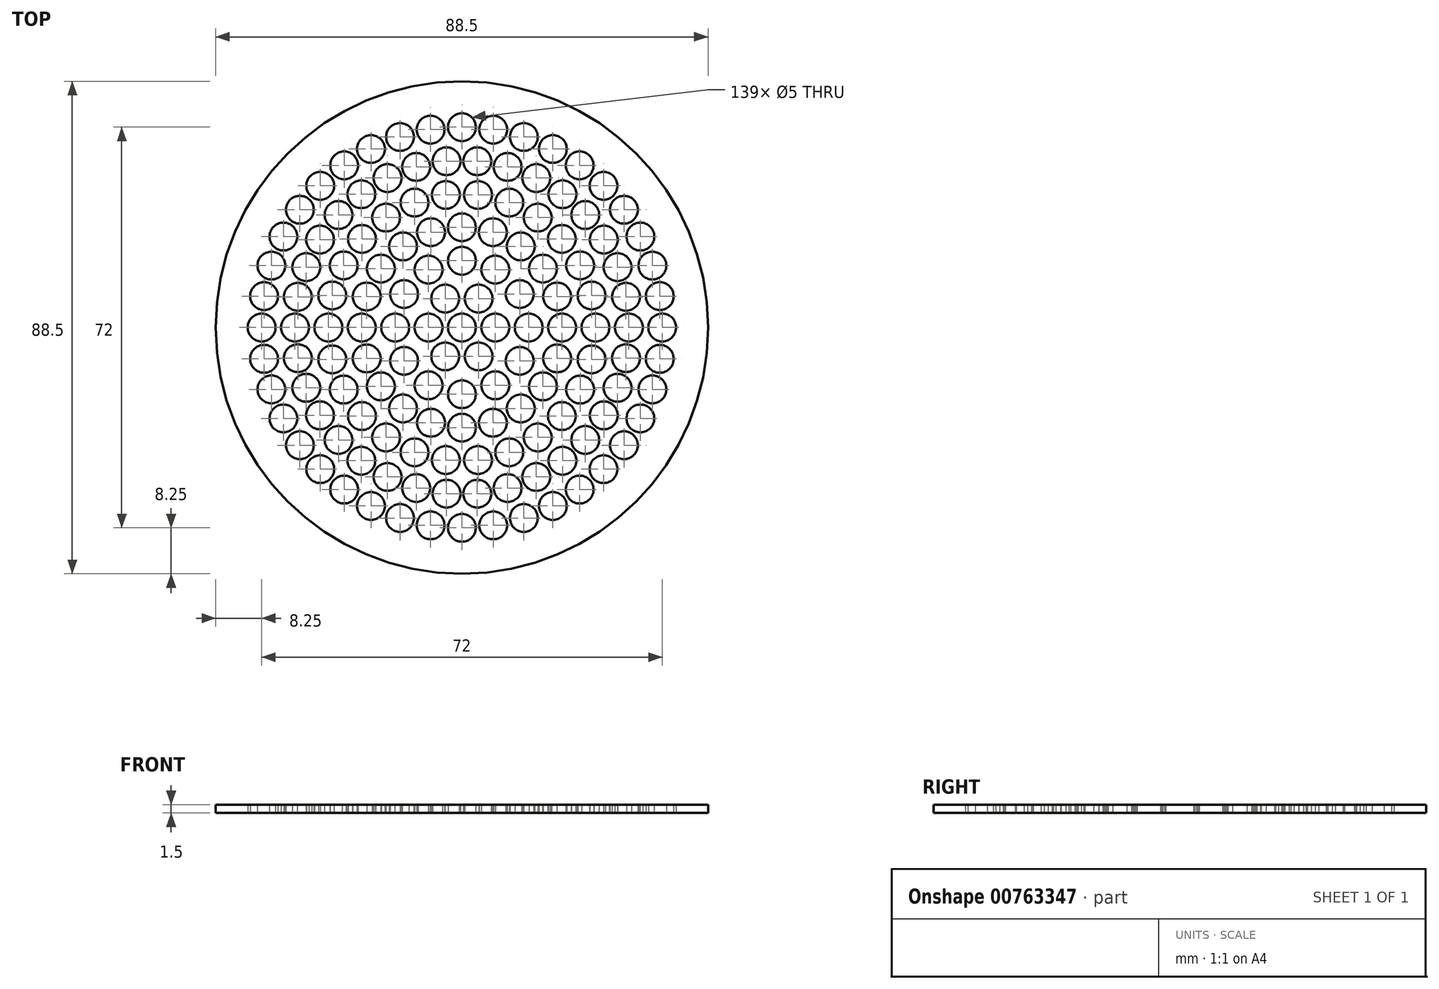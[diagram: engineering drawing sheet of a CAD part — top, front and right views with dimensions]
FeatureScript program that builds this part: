
annotation { "Feature Type Name" : "Feature", "Feature Type Description" : "" }
export const myFeature = defineFeature(function(context is Context, id is Id, definition is map)
    precondition{}
    {
        {
            var Q0;
            Q0=qCreatedBy(makeId("Top.planeOp"),FACE);
            var sketch = newSketch(context, id + "F0", { "sketchPlane" : qUnion([Q0])});
            skCircle(sketch, "E0", {"center": v(0, 0) * mm, "radius": 44.25 * mm});
            skCircle(sketch, "E1", {"center": v(0, 0) * mm, "radius": 2.5 * mm});
            skCircle(sketch, "E2.1.0.0", {"center": v(6, 0) * mm, "radius": 2.5 * mm});
            skCircle(sketch, "E2.2.0.0", {"center": v(12, 0) * mm, "radius": 2.5 * mm});
            skCircle(sketch, "E2.3.0.0", {"center": v(18, 0) * mm, "radius": 2.5 * mm});
            skCircle(sketch, "E2.4.0.0", {"center": v(24, 0) * mm, "radius": 2.5 * mm});
            skCircle(sketch, "E2.5.0.0", {"center": v(30, 0) * mm, "radius": 2.5 * mm});
            skCircle(sketch, "E2.6.0.0", {"center": v(36, 0) * mm, "radius": 2.5 * mm});
            skLineSegment(sketch, "E2.direction1", {"start": v(0, 0) * mm, "end": v(6, 0) * mm, "construction": true});
            skCircle(sketch, "E3.1.0", {"center": v(3, 5.2) * mm, "radius": 2.5 * mm});
            skCircle(sketch, "E3.2.0", {"center": v(-3, 5.2) * mm, "radius": 2.5 * mm});
            skCircle(sketch, "E3.3.0", {"center": v(-6, 0) * mm, "radius": 2.5 * mm});
            skCircle(sketch, "E3.4.0", {"center": v(-3, -5.2) * mm, "radius": 2.5 * mm});
            skCircle(sketch, "E4.1.0", {"center": v(10.4, 6) * mm, "radius": 2.5 * mm});
            skCircle(sketch, "E4.2.0", {"center": v(6, 10.4) * mm, "radius": 2.5 * mm});
            skCircle(sketch, "E4.3.0", {"center": v(0, 12) * mm, "radius": 2.5 * mm});
            skCircle(sketch, "E4.4.0", {"center": v(-6, 10.4) * mm, "radius": 2.5 * mm});
            skCircle(sketch, "E4.5.0", {"center": v(-10.4, 6) * mm, "radius": 2.5 * mm});
            skCircle(sketch, "E4.6.0", {"center": v(-12, 0) * mm, "radius": 2.5 * mm});
            skCircle(sketch, "E4.7.0", {"center": v(-10.4, -6) * mm, "radius": 2.5 * mm});
            skCircle(sketch, "E4.8.0", {"center": v(-6, -10.4) * mm, "radius": 2.5 * mm});
            skCircle(sketch, "E4.9.0", {"center": v(0, -12) * mm, "radius": 2.5 * mm});
            skCircle(sketch, "E5.1.5.0", {"center": v(3, -5.2) * mm, "radius": 2.5 * mm});
            skCircle(sketch, "E6.1.10.0", {"center": v(6, -10.4) * mm, "radius": 2.5 * mm});
            skCircle(sketch, "E6.1.11.0", {"center": v(10.4, -6) * mm, "radius": 2.5 * mm});
            skCircle(sketch, "E7.1.0", {"center": v(17.12, 5.56) * mm, "radius": 2.5 * mm});
            skCircle(sketch, "E7.2.0", {"center": v(14.56, 10.58) * mm, "radius": 2.5 * mm});
            skCircle(sketch, "E7.3.0", {"center": v(10.58, 14.56) * mm, "radius": 2.5 * mm});
            skCircle(sketch, "E7.4.0", {"center": v(5.56, 17.12) * mm, "radius": 2.5 * mm});
            skCircle(sketch, "E7.5.0", {"center": v(0, 18) * mm, "radius": 2.5 * mm});
            skCircle(sketch, "E7.6.0", {"center": v(-5.56, 17.12) * mm, "radius": 2.5 * mm});
            skCircle(sketch, "E7.7.0", {"center": v(-10.58, 14.56) * mm, "radius": 2.5 * mm});
            skCircle(sketch, "E7.8.0", {"center": v(-14.56, 10.58) * mm, "radius": 2.5 * mm});
            skCircle(sketch, "E7.9.0", {"center": v(-17.12, 5.56) * mm, "radius": 2.5 * mm});
            skCircle(sketch, "E7.10.0", {"center": v(-18, 0) * mm, "radius": 2.5 * mm});
            skCircle(sketch, "E7.11.0", {"center": v(-17.12, -5.56) * mm, "radius": 2.5 * mm});
            skCircle(sketch, "E7.12.0", {"center": v(-14.56, -10.58) * mm, "radius": 2.5 * mm});
            skCircle(sketch, "E7.13.0", {"center": v(-10.58, -14.56) * mm, "radius": 2.5 * mm});
            skCircle(sketch, "E7.14.0", {"center": v(-5.56, -17.12) * mm, "radius": 2.5 * mm});
            skCircle(sketch, "E7.15.0", {"center": v(0, -18) * mm, "radius": 2.5 * mm});
            skCircle(sketch, "E7.16.0", {"center": v(5.56, -17.12) * mm, "radius": 2.5 * mm});
            skCircle(sketch, "E7.17.0", {"center": v(10.58, -14.56) * mm, "radius": 2.5 * mm});
            skCircle(sketch, "E7.18.0", {"center": v(14.56, -10.58) * mm, "radius": 2.5 * mm});
            skCircle(sketch, "E7.19.0", {"center": v(17.12, -5.56) * mm, "radius": 2.5 * mm});
            skCircle(sketch, "E8.1.0", {"center": v(23.3, 5.74) * mm, "radius": 2.5 * mm});
            skCircle(sketch, "E8.2.0", {"center": v(21.25, 11.15) * mm, "radius": 2.5 * mm});
            skCircle(sketch, "E8.3.0", {"center": v(17.96, 15.91) * mm, "radius": 2.5 * mm});
            skCircle(sketch, "E8.4.0", {"center": v(13.63, 19.75) * mm, "radius": 2.5 * mm});
            skCircle(sketch, "E8.5.0", {"center": v(8.51, 22.44) * mm, "radius": 2.5 * mm});
            skCircle(sketch, "E8.6.0", {"center": v(2.9, 23.83) * mm, "radius": 2.5 * mm});
            skCircle(sketch, "E8.7.0", {"center": v(-2.9, 23.83) * mm, "radius": 2.5 * mm});
            skCircle(sketch, "E8.8.0", {"center": v(-8.51, 22.44) * mm, "radius": 2.5 * mm});
            skCircle(sketch, "E8.9.0", {"center": v(-13.63, 19.75) * mm, "radius": 2.5 * mm});
            skCircle(sketch, "E8.10.0", {"center": v(-17.96, 15.91) * mm, "radius": 2.5 * mm});
            skCircle(sketch, "E8.11.0", {"center": v(-21.25, 11.15) * mm, "radius": 2.5 * mm});
            skCircle(sketch, "E8.12.0", {"center": v(-23.3, 5.74) * mm, "radius": 2.5 * mm});
            skCircle(sketch, "E8.13.0", {"center": v(-24, 0) * mm, "radius": 2.5 * mm});
            skCircle(sketch, "E8.14.0", {"center": v(-23.3, -5.74) * mm, "radius": 2.5 * mm});
            skCircle(sketch, "E8.15.0", {"center": v(-21.25, -11.15) * mm, "radius": 2.5 * mm});
            skCircle(sketch, "E8.16.0", {"center": v(-17.96, -15.91) * mm, "radius": 2.5 * mm});
            skCircle(sketch, "E8.17.0", {"center": v(-13.63, -19.75) * mm, "radius": 2.5 * mm});
            skCircle(sketch, "E8.18.0", {"center": v(-8.51, -22.44) * mm, "radius": 2.5 * mm});
            skCircle(sketch, "E8.19.0", {"center": v(-2.9, -23.83) * mm, "radius": 2.5 * mm});
            skCircle(sketch, "E8.20.0", {"center": v(2.9, -23.83) * mm, "radius": 2.5 * mm});
            skCircle(sketch, "E8.21.0", {"center": v(8.51, -22.44) * mm, "radius": 2.5 * mm});
            skCircle(sketch, "E8.22.0", {"center": v(13.63, -19.75) * mm, "radius": 2.5 * mm});
            skCircle(sketch, "E8.23.0", {"center": v(17.96, -15.91) * mm, "radius": 2.5 * mm});
            skCircle(sketch, "E8.24.0", {"center": v(21.25, -11.15) * mm, "radius": 2.5 * mm});
            skCircle(sketch, "E8.25.0", {"center": v(23.3, -5.74) * mm, "radius": 2.5 * mm});
            skCircle(sketch, "E9.1.0", {"center": v(29.49, 5.51) * mm, "radius": 2.5 * mm});
            skCircle(sketch, "E9.2.0", {"center": v(27.97, 10.84) * mm, "radius": 2.5 * mm});
            skCircle(sketch, "E9.3.0", {"center": v(25.5, 15.8) * mm, "radius": 2.5 * mm});
            skCircle(sketch, "E9.4.0", {"center": v(22.17, 20.21) * mm, "radius": 2.5 * mm});
            skCircle(sketch, "E9.5.0", {"center": v(18.08, 23.94) * mm, "radius": 2.5 * mm});
            skCircle(sketch, "E9.6.0", {"center": v(13.37, 26.85) * mm, "radius": 2.5 * mm});
            skCircle(sketch, "E9.7.0", {"center": v(8.2, 28.85) * mm, "radius": 2.5 * mm});
            skCircle(sketch, "E9.8.0", {"center": v(2.77, 29.87) * mm, "radius": 2.5 * mm});
            skCircle(sketch, "E9.9.0", {"center": v(-2.77, 29.87) * mm, "radius": 2.5 * mm});
            skCircle(sketch, "E9.10.0", {"center": v(-8.2, 28.85) * mm, "radius": 2.5 * mm});
            skCircle(sketch, "E9.11.0", {"center": v(-13.37, 26.85) * mm, "radius": 2.5 * mm});
            skCircle(sketch, "E9.12.0", {"center": v(-18.08, 23.94) * mm, "radius": 2.5 * mm});
            skCircle(sketch, "E9.13.0", {"center": v(-22.17, 20.21) * mm, "radius": 2.5 * mm});
            skCircle(sketch, "E9.14.0", {"center": v(-25.5, 15.8) * mm, "radius": 2.5 * mm});
            skCircle(sketch, "E9.15.0", {"center": v(-27.97, 10.84) * mm, "radius": 2.5 * mm});
            skCircle(sketch, "E9.16.0", {"center": v(-29.49, 5.51) * mm, "radius": 2.5 * mm});
            skCircle(sketch, "E9.17.0", {"center": v(-30, 0) * mm, "radius": 2.5 * mm});
            skCircle(sketch, "E9.18.0", {"center": v(-29.49, -5.51) * mm, "radius": 2.5 * mm});
            skCircle(sketch, "E9.19.0", {"center": v(-27.97, -10.84) * mm, "radius": 2.5 * mm});
            skCircle(sketch, "E9.20.0", {"center": v(-25.5, -15.8) * mm, "radius": 2.5 * mm});
            skCircle(sketch, "E9.21.0", {"center": v(-22.17, -20.21) * mm, "radius": 2.5 * mm});
            skCircle(sketch, "E9.22.0", {"center": v(-18.08, -23.94) * mm, "radius": 2.5 * mm});
            skCircle(sketch, "E9.23.0", {"center": v(-13.37, -26.85) * mm, "radius": 2.5 * mm});
            skCircle(sketch, "E9.24.0", {"center": v(-8.2, -28.85) * mm, "radius": 2.5 * mm});
            skCircle(sketch, "E9.25.0", {"center": v(-2.77, -29.87) * mm, "radius": 2.5 * mm});
            skCircle(sketch, "E9.26.0", {"center": v(2.77, -29.87) * mm, "radius": 2.5 * mm});
            skCircle(sketch, "E9.27.0", {"center": v(8.2, -28.85) * mm, "radius": 2.5 * mm});
            skCircle(sketch, "E9.28.0", {"center": v(13.37, -26.85) * mm, "radius": 2.5 * mm});
            skCircle(sketch, "E9.29.0", {"center": v(18.08, -23.94) * mm, "radius": 2.5 * mm});
            skCircle(sketch, "E9.30.0", {"center": v(22.17, -20.21) * mm, "radius": 2.5 * mm});
            skCircle(sketch, "E9.31.0", {"center": v(25.5, -15.8) * mm, "radius": 2.5 * mm});
            skCircle(sketch, "E9.32.0", {"center": v(27.97, -10.84) * mm, "radius": 2.5 * mm});
            skCircle(sketch, "E9.33.0", {"center": v(29.49, -5.51) * mm, "radius": 2.5 * mm});
            skCircle(sketch, "E10.1.0", {"center": v(35.56, 5.63) * mm, "radius": 2.5 * mm});
            skCircle(sketch, "E10.2.0", {"center": v(34.24, 11.12) * mm, "radius": 2.5 * mm});
            skCircle(sketch, "E10.3.0", {"center": v(32.08, 16.34) * mm, "radius": 2.5 * mm});
            skCircle(sketch, "E10.4.0", {"center": v(29.12, 21.16) * mm, "radius": 2.5 * mm});
            skCircle(sketch, "E10.5.0", {"center": v(25.46, 25.46) * mm, "radius": 2.5 * mm});
            skCircle(sketch, "E10.6.0", {"center": v(21.16, 29.12) * mm, "radius": 2.5 * mm});
            skCircle(sketch, "E10.7.0", {"center": v(16.34, 32.08) * mm, "radius": 2.5 * mm});
            skCircle(sketch, "E10.8.0", {"center": v(11.12, 34.24) * mm, "radius": 2.5 * mm});
            skCircle(sketch, "E10.9.0", {"center": v(5.63, 35.56) * mm, "radius": 2.5 * mm});
            skCircle(sketch, "E10.10.0", {"center": v(0, 36) * mm, "radius": 2.5 * mm});
            skCircle(sketch, "E10.11.0", {"center": v(-5.63, 35.56) * mm, "radius": 2.5 * mm});
            skCircle(sketch, "E10.12.0", {"center": v(-11.12, 34.24) * mm, "radius": 2.5 * mm});
            skCircle(sketch, "E10.13.0", {"center": v(-16.34, 32.08) * mm, "radius": 2.5 * mm});
            skCircle(sketch, "E10.14.0", {"center": v(-21.16, 29.12) * mm, "radius": 2.5 * mm});
            skCircle(sketch, "E10.15.0", {"center": v(-25.46, 25.46) * mm, "radius": 2.5 * mm});
            skCircle(sketch, "E10.16.0", {"center": v(-29.12, 21.16) * mm, "radius": 2.5 * mm});
            skCircle(sketch, "E10.17.0", {"center": v(-32.08, 16.34) * mm, "radius": 2.5 * mm});
            skCircle(sketch, "E10.18.0", {"center": v(-34.24, 11.12) * mm, "radius": 2.5 * mm});
            skCircle(sketch, "E10.19.0", {"center": v(-35.56, 5.63) * mm, "radius": 2.5 * mm});
            skCircle(sketch, "E10.20.0", {"center": v(-36, 0) * mm, "radius": 2.5 * mm});
            skCircle(sketch, "E10.21.0", {"center": v(-35.56, -5.63) * mm, "radius": 2.5 * mm});
            skCircle(sketch, "E10.22.0", {"center": v(-34.24, -11.12) * mm, "radius": 2.5 * mm});
            skCircle(sketch, "E10.23.0", {"center": v(-32.08, -16.34) * mm, "radius": 2.5 * mm});
            skCircle(sketch, "E10.24.0", {"center": v(-29.12, -21.16) * mm, "radius": 2.5 * mm});
            skCircle(sketch, "E10.25.0", {"center": v(-25.46, -25.46) * mm, "radius": 2.5 * mm});
            skCircle(sketch, "E10.26.0", {"center": v(-21.16, -29.12) * mm, "radius": 2.5 * mm});
            skCircle(sketch, "E10.27.0", {"center": v(-16.34, -32.08) * mm, "radius": 2.5 * mm});
            skCircle(sketch, "E10.28.0", {"center": v(-11.12, -34.24) * mm, "radius": 2.5 * mm});
            skCircle(sketch, "E10.29.0", {"center": v(-5.63, -35.56) * mm, "radius": 2.5 * mm});
            skCircle(sketch, "E10.30.0", {"center": v(0, -36) * mm, "radius": 2.5 * mm});
            skCircle(sketch, "E10.31.0", {"center": v(5.63, -35.56) * mm, "radius": 2.5 * mm});
            skCircle(sketch, "E10.32.0", {"center": v(11.12, -34.24) * mm, "radius": 2.5 * mm});
            skCircle(sketch, "E10.33.0", {"center": v(16.34, -32.08) * mm, "radius": 2.5 * mm});
            skCircle(sketch, "E10.34.0", {"center": v(21.16, -29.12) * mm, "radius": 2.5 * mm});
            skCircle(sketch, "E10.35.0", {"center": v(25.46, -25.46) * mm, "radius": 2.5 * mm});
            skCircle(sketch, "E10.36.0", {"center": v(29.12, -21.16) * mm, "radius": 2.5 * mm});
            skCircle(sketch, "E10.37.0", {"center": v(32.08, -16.34) * mm, "radius": 2.5 * mm});
            skCircle(sketch, "E10.38.0", {"center": v(34.24, -11.12) * mm, "radius": 2.5 * mm});
            skCircle(sketch, "E10.39.0", {"center": v(35.56, -5.63) * mm, "radius": 2.5 * mm});
            skSolve(sketch);
        }
        {
            var Q0;
            Q0 = qSketchRegion(id + "F0", true);
            extrude(context, id + "F1", {"entities" : qUnion([Q0]), "depth" : 1.5 * mm, "offsetDistance" : 25 * mm});
        }
    });
